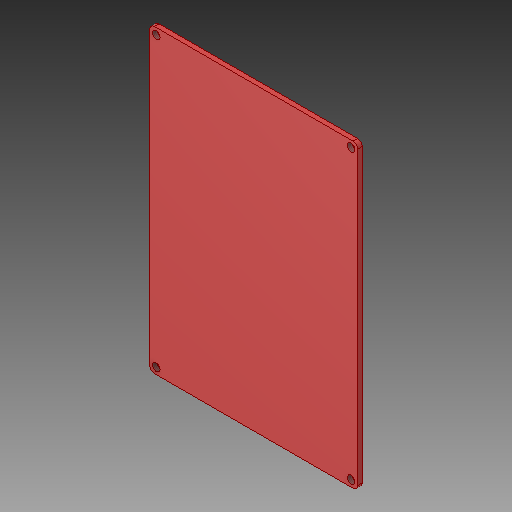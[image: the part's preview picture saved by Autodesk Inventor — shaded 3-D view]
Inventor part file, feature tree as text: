
AUTODESK INVENTOR PART (.ipt)
format: ipt  version: 2018 (Build 220112000, 112)  size: 121,344 bytes
history: native  units: in
note: dims shown in document units (in); Inventor stores cm internally (conversion verified against a paired STEP export)
features: reference x8, other x3, sketch x2, extrude x1, hole x1, fillet x1
ambient origin geometry x8: Origin, YZ Plane, XZ Plane, XY Plane, X Axis, Y Axis, Z Axis, Center Point
bodies: Solid1 (feature_tree)
feature tree (16):
  extrude  "Extrusion1"  Depth=0.15in
  hole  "Hole1"  [1 undecoded]
  fillet  "Fillet1"  Radius=0.25in
  sketch  "Sketch1"  dims[d0=0.15in d1=0.15in]
  reference  "Reference1"
  reference  "Reference2"
  reference  "Reference3"
  reference  "Reference4"
  sketch  "Sketch2"  dims[d2=0.15in d3=0.15in d4=0.25in d5=0.0in d6=0.417in d7=1.0in d8=0.375in d9=0.25in d10=0.5635in d11=1.385in d12=0.8108in d13=0.25in]
  reference  "Reference5"
  reference  "Reference6"
  reference  "Reference7"
  reference  "Reference8"
  other  "<userpath>\Desktop\School\CADD 2\Ferris Wheel\Left Door.iam"
  other  "Left Door.iam"
  other  "Door Frame:1"
note: 1 required parameter value undecoded (feature->parameter linkage not recoverable at this tier; creation-order binding heuristic only, values carry confidence <= 0.55)
